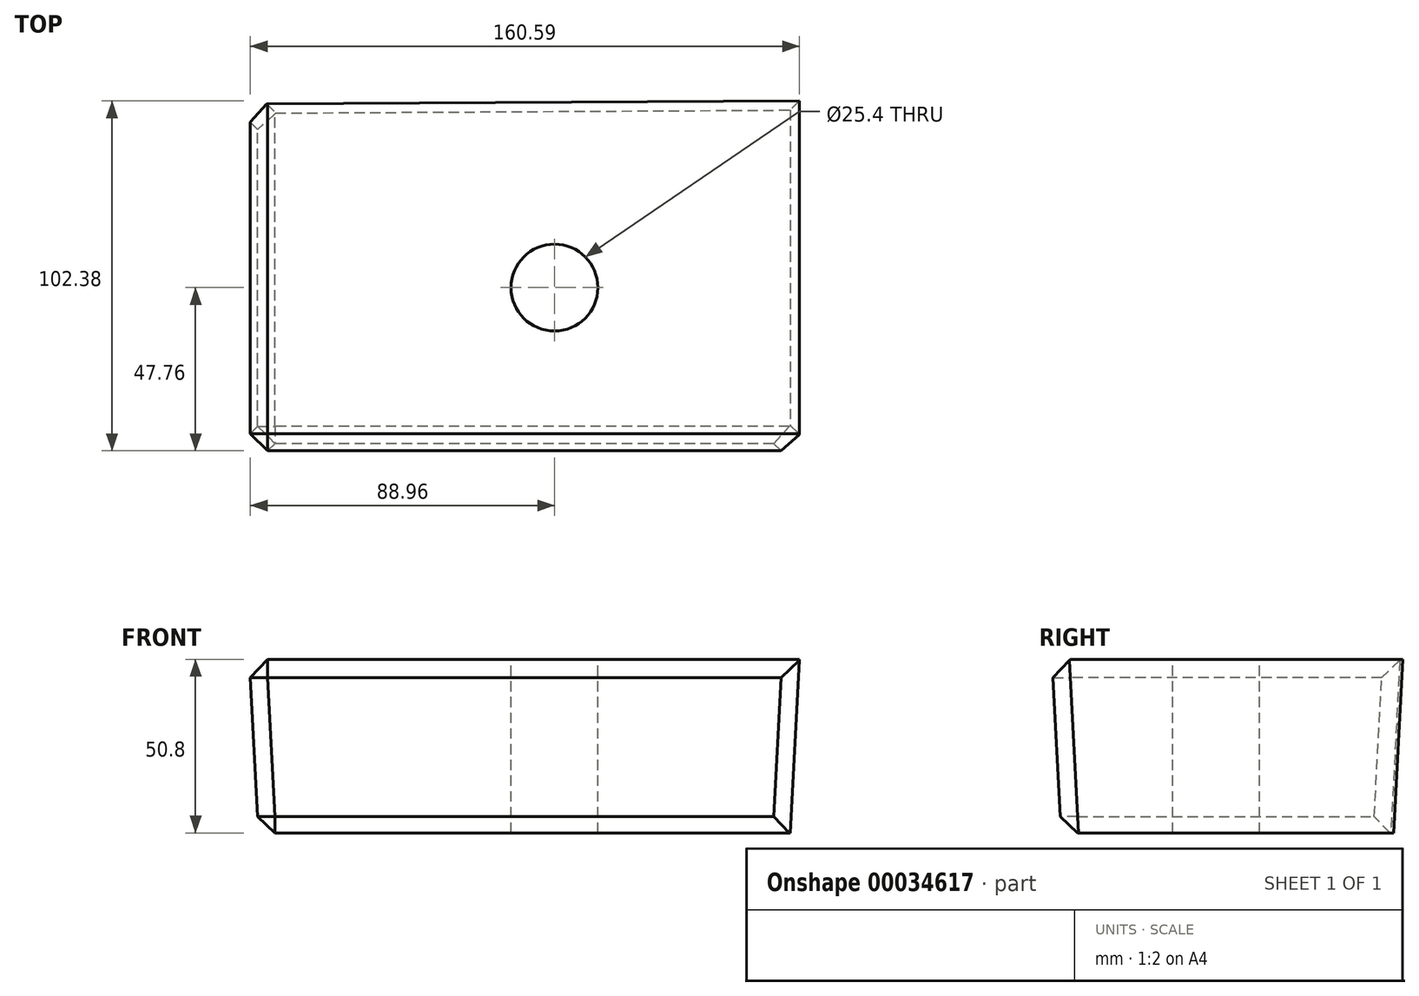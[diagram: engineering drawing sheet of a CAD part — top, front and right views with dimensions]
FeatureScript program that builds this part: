
annotation { "Feature Type Name" : "Feature", "Feature Type Description" : "" }
export const myFeature = defineFeature(function(context is Context, id is Id, definition is map)
    precondition{}
    {
        {
            var Q0;
            Q0=qCreatedBy(makeId("Top.planeOp"),FACE);
            var sketch = newSketch(context, id + "F0", { "sketchPlane" : qUnion([Q0])});
            skLineSegment(sketch, "E0", {"start": v(-86.58, 51.05) * mm, "end": v(-86.58, -45.38) * mm});
            skLineSegment(sketch, "E1", {"start": v(-86.58, -45.38) * mm, "end": v(68.96, -45.38) * mm});
            skLineSegment(sketch, "E2", {"start": v(68.96, -45.38) * mm, "end": v(68.96, 51.95) * mm});
            skLineSegment(sketch, "E3", {"start": v(68.96, 51.95) * mm, "end": v(-86.58, 51.05) * mm});
            skSolve(sketch);
        }
        {
            var Q0;
            Q0=makeQuery(id+"F0.imprint","IMPRINT",FACE,{"disambiguationData":[TD([[makeQuery(id+"F0.imprint","IMPRINT",EDGE,{"derivedFrom":sQuery(id+"F0.wireOp",EDGE,"E0")}),1.0]])]});
            extrude(context, id + "F1", {"entities" : qUnion([Q0]), "depth" : 50.8 * mm, "hasDraft" : true, "draftAngle" : 3 * degree});
        }
        {
            var Q0;
            Q0=makeQuery(id+"F1.opExtrude","SWEPT_FACE",FACE,{"disambiguationData":[OSD([sQuery(id+"F0.wireOp",EDGE,"E1")])]});
            var Q1;
            Q1=makeQuery(id+"F1.opExtrude","SWEPT_FACE",FACE,{"disambiguationData":[OSD([sQuery(id+"F0.wireOp",EDGE,"E0")])]});
            chamfer(context, id + "F2", {"entities" : qUnion([Q0, Q1]), "width" : 5.08 * mm, "tangentPropagation" : true});
        }
        {
            var Q0;
            Q0=makeQuery(id+"F1.opExtrude","CAP_FACE",FACE,{"disambiguationData":[OSD([sQuery(id+"F0.wireOp",EDGE,"E0"),sQuery(id+"F0.wireOp",EDGE,"E1"),sQuery(id+"F0.wireOp",EDGE,"E2"),sQuery(id+"F0.wireOp",EDGE,"E3")])],"isStart":false});
            var sketch = newSketch(context, id + "F3", { "sketchPlane" : qUnion([Q0])});
            skSolve(sketch);
        }
        {
            var Q0;
            {var subQ1=sQuery(id+"F0.wireOp",EDGE,"E2");Q0=makeQuery(id+"F3.imprint","IMPRINT",FACE,{"disambiguationData":[TD([[makeQuery(id+"F3.imprint","IMPRINT",EDGE,{"derivedFrom":makeQuery(id+"F1.opExtrude","CAP_EDGE",EDGE,{"disambiguationData":[OSD([subQ1])],"isStart":false})}),1.0]])]});}
            var sketch = newSketch(context, id + "F4", { "sketchPlane" : qUnion([Q0])});
            skPoint(sketch, "E4", {"position": v(0, 0) * mm});
            skSolve(sketch);
        }
        {
            var Q0;
            Q0=sQuery(id+"F4.wireOp",VERTEX,"E4");
            var Q1;
            Q1=makeQuery(id+"F1.opExtrude","SWEPT_BODY",BODY,{"disambiguationData":[OSD([sQuery(id+"F0.wireOp",EDGE,"E0"),sQuery(id+"F0.wireOp",EDGE,"E1"),sQuery(id+"F0.wireOp",EDGE,"E2"),sQuery(id+"F0.wireOp",EDGE,"E3")])]});
            hole(context, id + "F5", {"style" : HoleStyle.SIMPLE, "holeDiameter" : 25.4 * mm, "endStyle" : HoleEndStyle.THROUGH, "locations" : qUnion([Q0]), "scope" : qUnion([Q1])});
        }
    });
